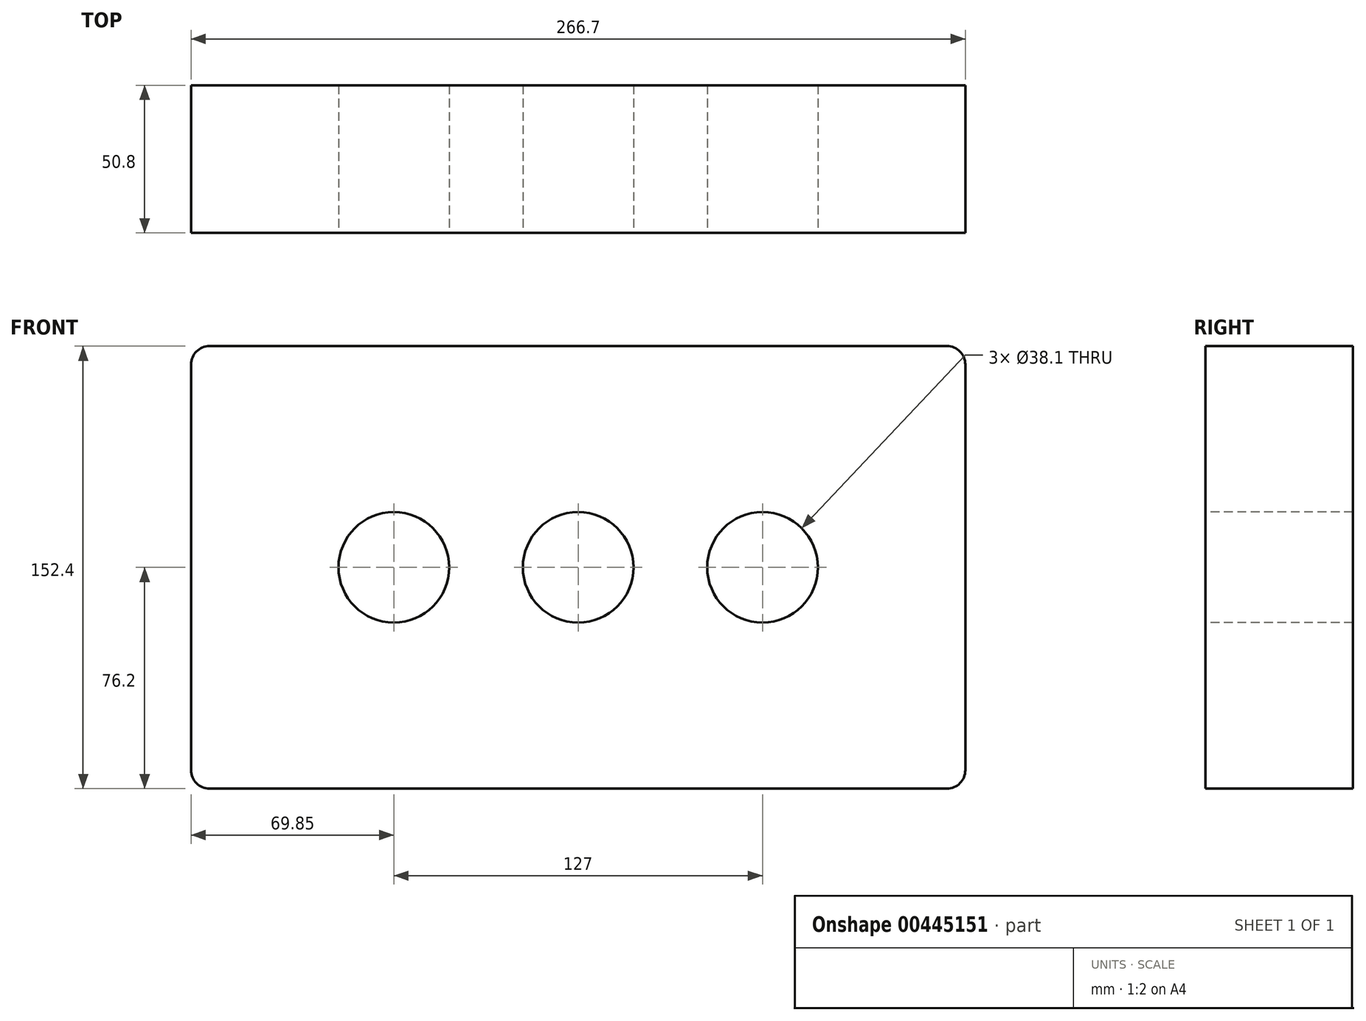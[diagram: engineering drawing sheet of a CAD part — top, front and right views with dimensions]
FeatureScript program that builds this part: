
annotation { "Feature Type Name" : "Feature", "Feature Type Description" : "" }
export const myFeature = defineFeature(function(context is Context, id is Id, definition is map)
    precondition{}
    {
        {
            var Q0;
            Q0=qCreatedBy(makeId("Front.planeOp"),FACE);
            var sketch = newSketch(context, id + "F0", { "sketchPlane" : qUnion([Q0])});
            skLineSegment(sketch, "E0.bottom", {"start": v(133.35, 76.2) * mm, "end": v(-133.35, 76.2) * mm});
            skLineSegment(sketch, "E0.top", {"start": v(133.35, -76.2) * mm, "end": v(-133.35, -76.2) * mm});
            skLineSegment(sketch, "E0.left", {"start": v(133.35, 76.2) * mm, "end": v(133.35, -76.2) * mm});
            skLineSegment(sketch, "E0.right", {"start": v(-133.35, 76.2) * mm, "end": v(-133.35, -76.2) * mm});
            skPoint(sketch, "E0.middle", {"position": v(0, 0) * mm});
            skSolve(sketch);
        }
        {
            var Q0;
            Q0=makeQuery(id+"F0.imprint","IMPRINT",FACE,{"disambiguationData":[TD([[makeQuery(id+"F0.imprint","IMPRINT",EDGE,{"derivedFrom":sQuery(id+"F0.wireOp",EDGE,"E0.bottom")}),1.0]])]});
            extrude(context, id + "F1", {"entities" : qUnion([Q0]), "depth" : 50.8 * mm});
        }
        {
            var Q0;
            Q0=makeQuery(id+"F1.opExtrude","CAP_FACE",FACE,{"disambiguationData":[OSD([sQuery(id+"F0.wireOp",EDGE,"E0.bottom"),sQuery(id+"F0.wireOp",EDGE,"E0.top"),sQuery(id+"F0.wireOp",EDGE,"E0.left"),sQuery(id+"F0.wireOp",EDGE,"E0.right")])],"isStart":false});
            var sketch = newSketch(context, id + "F2", { "sketchPlane" : qUnion([Q0])});
            skCircle(sketch, "E1", {"center": v(0, 0) * mm, "radius": 19.05 * mm});
            skLineSegment(sketch, "E2", {"start": v(-19.05, 0) * mm, "end": v(-44.45, 0) * mm});
            skLineSegment(sketch, "E3", {"start": v(19.05, 0) * mm, "end": v(44.45, 0) * mm});
            skLineSegment(sketch, "E4", {"start": v(-44.45, 0) * mm, "end": v(-63.5, 0) * mm});
            skLineSegment(sketch, "E5", {"start": v(44.45, 0) * mm, "end": v(63.5, 0) * mm});
            skCircle(sketch, "E6", {"center": v(63.5, 0) * mm, "radius": 19.05 * mm});
            skCircle(sketch, "E7", {"center": v(-63.5, 0) * mm, "radius": 19.05 * mm});
            skSolve(sketch);
        }
        {
            var Q0;
            Q0=makeQuery(id+"F2.imprint","IMPRINT",FACE,{"disambiguationData":[TD([[makeQuery(id+"F2.imprint","IMPRINT",EDGE,{"derivedFrom":sQuery(id+"F2.wireOp",EDGE,"E7")}),1.0]])]});
            var Q1;
            {var subQ0=sQuery(id+"F2.wireOp",EDGE,"E1");var subQ1=makeQuery(id+"F2.imprint","IMPRINT",VERTEX,{"disambiguationData":[OD(0.0)],"derivedFrom":subQ0});Q1=makeQuery(id+"F2.imprint","IMPRINT",FACE,{"disambiguationData":[TD([[makeQuery(id+"F2.imprint","IMPRINT",EDGE,{"disambiguationData":[TD([[subQ1,1.0]])],"derivedFrom":subQ0}),1.0]])]});}
            var Q2;
            Q2=makeQuery(id+"F2.imprint","IMPRINT",FACE,{"disambiguationData":[TD([[makeQuery(id+"F2.imprint","IMPRINT",EDGE,{"derivedFrom":sQuery(id+"F2.wireOp",EDGE,"E6")}),1.0]])]});
            extrude(context, id + "F3", {"entities" : qUnion([Q0, Q1, Q2]), "operationType" : NewBodyOperationType.REMOVE, "oppositeDirection" : true, "depth" : 76.2 * mm});
        }
        {
            var Q0;
            Q0=makeQuery(id+"F1.opExtrude","SWEPT_EDGE",EDGE,{"disambiguationData":[OSD([sQuery(id+"F0.wireOp",EDGE,"E0.bottom"),sQuery(id+"F0.wireOp",EDGE,"E0.left")])]});
            var Q1;
            Q1=makeQuery(id+"F1.opExtrude","SWEPT_EDGE",EDGE,{"disambiguationData":[OSD([sQuery(id+"F0.wireOp",EDGE,"E0.top"),sQuery(id+"F0.wireOp",EDGE,"E0.left")])]});
            var Q2;
            Q2=makeQuery(id+"F1.opExtrude","SWEPT_EDGE",EDGE,{"disambiguationData":[OSD([sQuery(id+"F0.wireOp",EDGE,"E0.bottom"),sQuery(id+"F0.wireOp",EDGE,"E0.right")])]});
            var Q3;
            Q3=makeQuery(id+"F1.opExtrude","SWEPT_EDGE",EDGE,{"disambiguationData":[OSD([sQuery(id+"F0.wireOp",EDGE,"E0.top"),sQuery(id+"F0.wireOp",EDGE,"E0.right")])]});
            fillet(context, id + "F4", {"entities" : qUnion([Q0, Q1, Q2, Q3]), "radius" : 6.35 * mm, "tangentPropagation" : true, "allowEdgeOverflow" : false});
        }
    });
